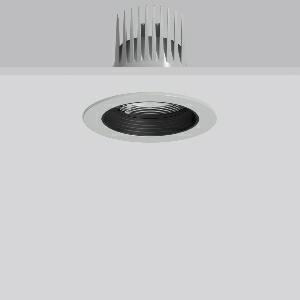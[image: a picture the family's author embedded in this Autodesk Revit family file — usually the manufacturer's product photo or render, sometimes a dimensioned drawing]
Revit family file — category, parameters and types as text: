
# Revit family: heledon_maxi_e_901774_004_3df4
name_source: partatom
category: Lighting Fixtures
units: mm (PartAtom-declared; Revit-internal decimal feet)

## family parameters
Cut with Voids When Loaded = No
Host = Face
Light Source = No
Part Type = Normal
Room Calculation Point = No
Round Connector Dimension = Use Diameter
Shared = No

## types (1)
- HELEDON maxi E (1 x LED Modul 932 fresh meat, 1800 lm, 3200)
    Apparent Load = 33 VA
    Approval mark = CE
    CIE Flux Codes = 97 100 100 100 100
    Color Rendering = 90
    Color Temperature = 3200
    Default Elevation = 1800 mm  [stored 5.90551 ft]
    Description = Series: HELEDON maxi
Round recessed downlight. Housing: die-cast aluminium, powder-coated. Black plastic ring and recessed LED to prevent glare from the side. Optical assembly with lens made of plastic (polycarbonate) for the best homogeneous light distribution - can be changed without tools. Special LED for illumination of meat included. Suitable for Recessed ceiling mounting. Installation without tools thanks to spring fastening system. Including separate LED converter with connecting cable 600 mm.High quality converter without flickering and stroboscopic effect. Through-wiring box (5 pole) available as accessory. The following accessories can be mounted without use of tools: interchangeable lenses, decorative glasses, honeycomb louvre, clear and frosted diffusers, white interchangeable plastic ring. 
Colour: silver
Diameter: 162 mm
Height: 3 mm
Cut-out diameter: 152 mm
Recess height: 200 mm
Luminaire: recess height: 135 mm
Lamp: LED
Socket: without socket
Colour temperature: fresh meat
System power: 33 W
Rated luminous flux: 1800 lm
Luminous efficiency: 55 lm/W
Control gear: Regulated power supply
Protection class: II
Type of protection: IP 20
    Height = 0 mm  [stored 0 ft]
    Lamp = 1 x LED Modul 932 fresh meat
    Lamp Light Flux = 1800 lm
    Lamp count = 1
    Length = 162 mm
    Lifetime = 50000 h
    Luminous efficacy = 55 lm/W
    Manufacturer = RZB
    ModVariant = No
    Model = 901774.004
    Mounting Place = Ceiling
    Mounting Type = Recessed
    Number of Poles = 1
    OnlyDefault = Yes
    Power Factor = 1
    Product Name = HELEDON maxi E
    Product group = Recessed downlights
    ProductGroupID = 402
    Protection Class = Protection class II
    Protection Degree = IP 20
    RLX_Detail_Level = 1
    RLX_Emergency_Light_Flux = 0 lm
    RLX_Emergency_Type = 0
    RLX_Emergency_Type_DB = No
    RlxData = <blob elided: 118785 chars, md5=938394b1>
    Socket = socket
    Standby Power = 0 W
    System Light Flux = 1800 lm
    System Power = 33 W
    Type Comments = Product without accessories
    Type Image = 901663.004.jpg
    URL = http://relux.com
    VarID = ---
    Voltage = 230 V
    Voltage Range = 220-240 V
    Weight = 0.00 kg
    Width = 0 mm  [stored 0 ft]

note: [stored X ft] marks values corroborated as IEEE doubles in the binary element streams (Revit-internal decimal feet)

## geometry (parser evidence)
native form markers: Blend x4, Sweep x11
no freeform markers — native parametric forms only
